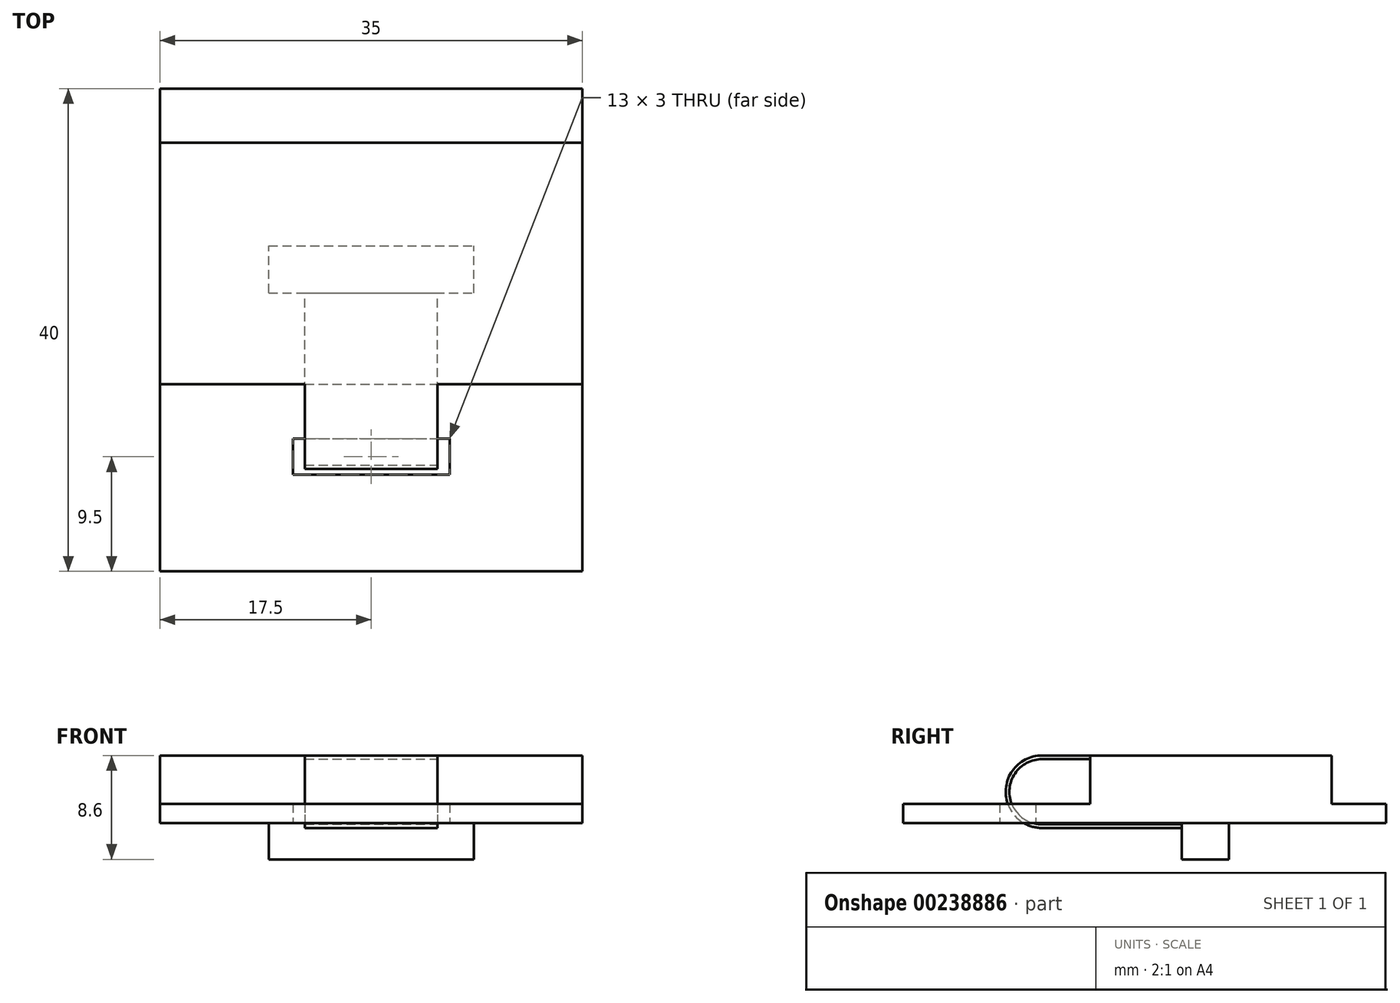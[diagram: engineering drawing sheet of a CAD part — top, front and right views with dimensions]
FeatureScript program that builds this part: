
annotation { "Feature Type Name" : "Feature", "Feature Type Description" : "" }
export const myFeature = defineFeature(function(context is Context, id is Id, definition is map)
    precondition{}
    {
        {
            var Q0;
            Q0=qCreatedBy(makeId("Top.planeOp"),FACE);
            var sketch = newSketch(context, id + "F0", { "sketchPlane" : qUnion([Q0])});
            skLineSegment(sketch, "E0.bottom", {"start": v(-17.5, 20) * mm, "end": v(17.5, 20) * mm});
            skLineSegment(sketch, "E0.top", {"start": v(-17.5, -20) * mm, "end": v(17.5, -20) * mm});
            skLineSegment(sketch, "E0.left", {"start": v(-17.5, 20) * mm, "end": v(-17.5, -20) * mm});
            skLineSegment(sketch, "E0.right", {"start": v(17.5, 20) * mm, "end": v(17.5, -20) * mm});
            skLineSegment(sketch, "E1.bottom", {"start": v(-6.5, -9) * mm, "end": v(6.5, -9) * mm});
            skLineSegment(sketch, "E1.top", {"start": v(-6.5, -12) * mm, "end": v(6.5, -12) * mm});
            skLineSegment(sketch, "E1.left", {"start": v(-6.5, -9) * mm, "end": v(-6.5, -12) * mm});
            skLineSegment(sketch, "E1.right", {"start": v(6.5, -9) * mm, "end": v(6.5, -12) * mm});
            skLineSegment(sketch, "E2", {"start": v(0, -20) * mm, "end": v(0, -12) * mm, "construction": true});
            skLineSegment(sketch, "E3", {"start": v(0, -20) * mm, "end": v(0, 20) * mm, "construction": true});
            skSolve(sketch);
        }
        {
            var Q0;
            Q0=qSketchRegion(id+"F0",true);
            var Q1;
            Q1=qConstructionFilter(qBodyType(qCreatedBy(id+"F0",EDGE),BodyType.WIRE),ConstructionObject.NO);
            extrude(context, id + "F1", {"entities" : qUnion([Q0]), "surfaceEntities" : qUnion([Q1]), "depth" : 1.6 * mm});
        }
        {
            var Q0;
            Q0=makeQuery(id+"F1.opExtrude","CAP_FACE",FACE,{"disambiguationData":[OSD([sQuery(id+"F0.wireOp",EDGE,"E0.bottom"),sQuery(id+"F0.wireOp",EDGE,"E0.top"),sQuery(id+"F0.wireOp",EDGE,"E0.left"),sQuery(id+"F0.wireOp",EDGE,"E0.right"),sQuery(id+"F0.wireOp",EDGE,"E1.bottom"),sQuery(id+"F0.wireOp",EDGE,"E1.top"),sQuery(id+"F0.wireOp",EDGE,"E1.left"),sQuery(id+"F0.wireOp",EDGE,"E1.right")])],"isStart":false});
            var sketch = newSketch(context, id + "F2", { "sketchPlane" : qUnion([Q0])});
            skLineSegment(sketch, "E4.bottom", {"start": v(-17.5, 15.5) * mm, "end": v(17.5, 15.5) * mm});
            skLineSegment(sketch, "E4.top", {"start": v(-17.5, -4.5) * mm, "end": v(17.5, -4.5) * mm});
            skLineSegment(sketch, "E4.left", {"start": v(-17.5, 15.5) * mm, "end": v(-17.5, -4.5) * mm});
            skLineSegment(sketch, "E4.right", {"start": v(17.5, 15.5) * mm, "end": v(17.5, -4.5) * mm});
            skLineSegment(sketch, "E5", {"start": v(-5.5, -4.5) * mm, "end": v(-5.5, -3.5) * mm});
            skLineSegment(sketch, "E6", {"start": v(-5.5, -3.5) * mm, "end": v(5.5, -3.5) * mm});
            skLineSegment(sketch, "E7", {"start": v(5.5, -3.5) * mm, "end": v(5.5, -4.5) * mm});
            skLineSegment(sketch, "E8", {"start": v(0, -4.5) * mm, "end": v(0, -3.5) * mm, "construction": true});
            skPoint(sketch, "E8.endSnap0", {"position": v(0, -4.5) * mm});
            skSolve(sketch);
        }
        {
            var Q0;
            Q0=qSketchRegion(id+"F2",true);
            extrude(context, id + "F3", {"entities" : qUnion([Q0]), "operationType" : NewBodyOperationType.ADD, "depth" : 4 * mm});
        }
        {
            var Q0;
            Q0=qCreatedBy(makeId("Right.planeOp"),FACE);
            var sketch = newSketch(context, id + "F4", { "sketchPlane" : qUnion([Q0])});
            skLineSegment(sketch, "E9", {"start": v(-4.5, 5.6) * mm, "end": v(-8.5, 5.6) * mm});
            skLineSegment(sketch, "E10", {"start": v(6.97, -0.4) * mm, "end": v(-8.5, -0.4) * mm});
            skLineSegment(sketch, "E11", {"start": v(-8.5, 5.6) * mm, "end": v(-8.5, -0.4) * mm, "construction": true});
            skArc(sketch, "E12", {"start": v(-8.5, 5.6) * mm, "mid": v(-11.5, 2.6) * mm, "end": v(-8.5, -0.4) * mm});
            skSolve(sketch);
        }
        {
            var Q0;
            Q0=makeQuery(id+"F3.opExtrude","SWEPT_FACE",FACE,{"disambiguationData":[OSD([sQuery(id+"F2.wireOp",EDGE,"E4.top")])]});
            var sketch = newSketch(context, id + "F5", { "sketchPlane" : qUnion([Q0])});
            skLineSegment(sketch, "E13.bottom", {"start": v(-5.5, 5.6) * mm, "end": v(5.5, 5.6) * mm});
            skLineSegment(sketch, "E13.top", {"start": v(-5.5, 5.3) * mm, "end": v(5.5, 5.3) * mm});
            skLineSegment(sketch, "E13.left", {"start": v(-5.5, 5.6) * mm, "end": v(-5.5, 5.3) * mm});
            skLineSegment(sketch, "E13.right", {"start": v(5.5, 5.6) * mm, "end": v(5.5, 5.3) * mm});
            skLineSegment(sketch, "E14", {"start": v(0, 1.6) * mm, "end": v(0, 5.3) * mm, "construction": true});
            skSolve(sketch);
        }
        {
            var Q0;
            Q0=makeQuery(id+"F5.imprint","IMPRINT",FACE,{"disambiguationData":[TD([[makeQuery(id+"F5.imprint","IMPRINT",EDGE,{"derivedFrom":sQuery(id+"F5.wireOp",EDGE,"E13.bottom")}),-1.0]])]});
            var Q1;
            Q1=qConstructionFilter(qBodyType(qCreatedBy(id+"F4",EDGE),BodyType.WIRE),ConstructionObject.NO);
            sweep(context, id + "F6", {"operationType" : NewBodyOperationType.ADD, "profiles" : qUnion([Q0]), "path" : qUnion([Q1])});
        }
        {
            var Q0;
            Q0=makeQuery(id+"F1.opExtrude","CAP_FACE",FACE,{"disambiguationData":[OSD([sQuery(id+"F0.wireOp",EDGE,"E0.bottom"),sQuery(id+"F0.wireOp",EDGE,"E0.top"),sQuery(id+"F0.wireOp",EDGE,"E0.left"),sQuery(id+"F0.wireOp",EDGE,"E0.right"),sQuery(id+"F0.wireOp",EDGE,"E1.bottom"),sQuery(id+"F0.wireOp",EDGE,"E1.top"),sQuery(id+"F0.wireOp",EDGE,"E1.left"),sQuery(id+"F0.wireOp",EDGE,"E1.right")])],"isStart":true});
            var sketch = newSketch(context, id + "F7", { "sketchPlane" : qUnion([Q0])});
            skLineSegment(sketch, "E15.bottom", {"start": v(-8.5, -3.07) * mm, "end": v(8.5, -3.07) * mm});
            skLineSegment(sketch, "E15.top", {"start": v(-8.5, -6.97) * mm, "end": v(8.5, -6.97) * mm});
            skLineSegment(sketch, "E15.left", {"start": v(-8.5, -3.07) * mm, "end": v(-8.5, -6.98) * mm});
            skLineSegment(sketch, "E15.right", {"start": v(8.5, -3.07) * mm, "end": v(8.5, -6.97) * mm});
            skLineSegment(sketch, "E16", {"start": v(0, 0) * mm, "end": v(0, -3.07) * mm, "construction": true});
            skSolve(sketch);
        }
        {
            var Q0;
            Q0=makeQuery(id+"F7.imprint","IMPRINT",FACE,{"disambiguationData":[TD([[makeQuery(id+"F7.imprint","IMPRINT",EDGE,{"derivedFrom":sQuery(id+"F7.wireOp",EDGE,"E15.bottom")}),-1.0]])]});
            extrude(context, id + "F8", {"entities" : qUnion([Q0]), "operationType" : NewBodyOperationType.ADD, "depth" : 3 * mm});
        }
    });
